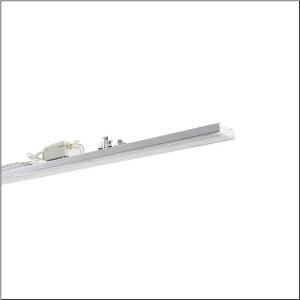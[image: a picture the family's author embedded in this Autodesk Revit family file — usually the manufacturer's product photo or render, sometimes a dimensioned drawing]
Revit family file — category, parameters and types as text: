
# Revit family: licross_r__21_recessed_ho_52tl12dn4axm_2663
name_source: partatom
category: Lighting Fixtures
units: mm (PartAtom-declared; Revit-internal decimal feet)

## family parameters
Cut with Voids When Loaded = No
Host = Face
Light Source = No
Part Type = Normal
Room Calculation Point = No
Round Connector Dimension = Use Diameter
Shared = No

## types (1)
- --- (1 x LED, 10000 lm, 54.6 W, 4000K)
    Apparent Load = 55 VA
    CIE Flux Codes = 69 91 98 100 100
    Color Rendering = 80
    Color Temperature = 4000K
    Default Elevation = 1800 mm
    Description = Licross® 21 Recessed HO, luminaire insert, of sheet steel, galvanised, coil coated, white, length: 1.500mm, width: 66mm, height: 67mm, LED rated luminous flux: 10.000lm, light colour: 840, control gear: DALI 2, with plug, 5-pole, with phase selection, mains connection: 220..240V, AC, 50/60Hz, rated input power: 55W, halogen-free wiring, primary optical cover: cover, of PMMA, light emission: direct distribution, primary light characteristic: symmetric, protection rating (complete): IP40, insulation class (complete): insulation class I (protective earthing), certification: CE, ENEC, VDE, UKCA, protection symbol: D if used in an environment without relevant dust loads with corresponding accessories, impact resistance: IK06, permissible ambient temperature for indoor applications: -25..+40°C, corresponds to IFS (International Featured Standards) requirements for safety and quality in the food industry, reducing of maximum allowable ambient temperature of 5°C with ceiling mounting, LABS conformity tested according to VDMA 24364:2018-05, packaging unit: 1 piece
    Height = 58 mm
    Lamp = 1 x LED
    Lamp Light Flux = 10000 lm
    Lamp Power = 54.6 W
    Lamp count = 1
    Length = 1500 mm
    Luminous efficacy = 183 lm/W
    Manufacturer = Siteco
    ModVariant = No
    Model = 52TL12DN4AXM
    Mounting Place = Ceiling
    Mounting Type = Pendant
    Number of Poles = 1
    OnlyDefault = Yes
    Power Factor = 1
    Product Name = Licross® 21 Recessed HO
    Product group = luminaire insert
    ProductGroupID = 901
    Protection Class = Protection class I
    Protection Degree = IP 40
    RLX_Detail_Level = 1
    RLX_Emergency_Light_Flux = 0 lm
    RLX_Emergency_Type = 0
    RLX_Emergency_Type_DB = No
    RlxData = <blob elided: 24401 chars, md5=8da4742b>
    Socket = socket
    Standby Power = 0 W
    System Light Flux = 10000 lm
    System Power = 55 W
    Type Comments = factory setting: luminous flux: 100 % | dim-lin: 254 | 313 mA
    Type Image = l_1296930.jpg
    URL = http://relux.com
    VarID = @adj_046557
    Voltage = 0 V
    Weight = 0.00 kg
    Width = 66 mm

## geometry (parser evidence)
native form markers: Blend x4, Sweep x10
no freeform markers — native parametric forms only
